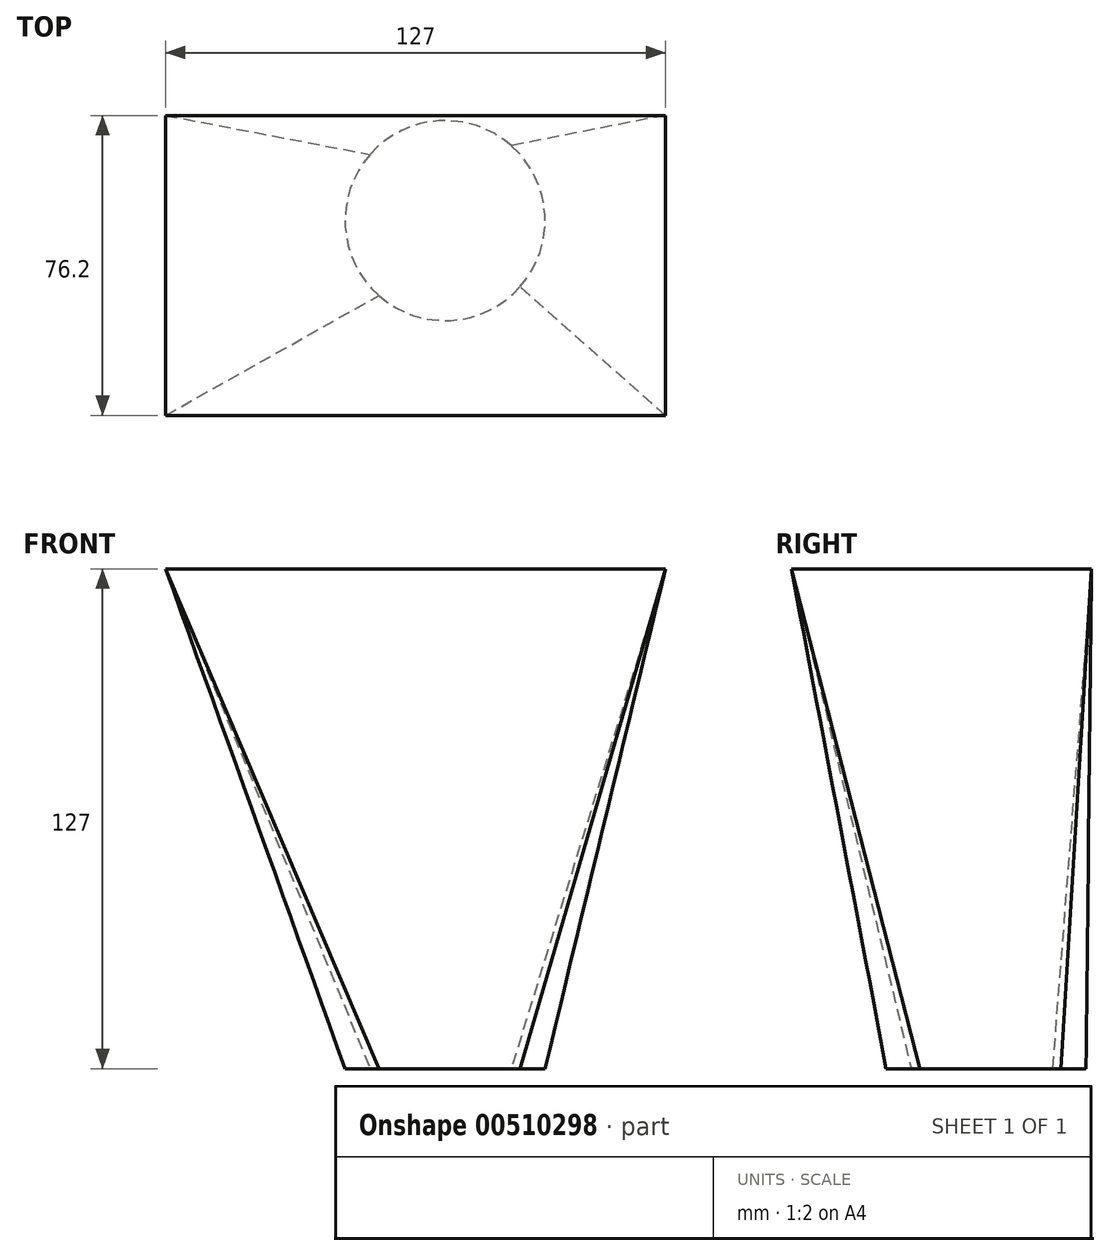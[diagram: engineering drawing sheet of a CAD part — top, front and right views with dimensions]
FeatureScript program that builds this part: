
annotation { "Feature Type Name" : "Feature", "Feature Type Description" : "" }
export const myFeature = defineFeature(function(context is Context, id is Id, definition is map)
    precondition{}
    {
        {
            var Q0;
            Q0=qCreatedBy(makeId("Top.planeOp"),FACE);
            var sketch = newSketch(context, id + "F0", { "sketchPlane" : qUnion([Q0])});
            skCircle(sketch, "E0", {"center": v(0, 11.37) * mm, "radius": 25.4 * mm});
            skSolve(sketch);
        }
        {
            var Q0;
            Q0=qCreatedBy(makeId("Top.planeOp"),FACE);
            cPlane(context, id + "F1", {"entities" : qUnion([Q0]), "cplaneType" : CPlaneType.OFFSET, "offset" : 127 * mm, "width" : 152.4 * mm, "height" : 152.4 * mm});
        }
        {
            var Q0;
            Q0=qCreatedBy(id+"F1.planeOp",FACE);
            var sketch = newSketch(context, id + "F2", { "sketchPlane" : qUnion([Q0])});
            skLineSegment(sketch, "E1.bottom", {"start": v(56, -38.1) * mm, "end": v(-71, -38.1) * mm});
            skLineSegment(sketch, "E1.top", {"start": v(56, 38.1) * mm, "end": v(-71, 38.1) * mm});
            skLineSegment(sketch, "E1.left", {"start": v(56, -38.1) * mm, "end": v(56, 38.1) * mm});
            skLineSegment(sketch, "E1.right", {"start": v(-71, -38.1) * mm, "end": v(-71, 38.1) * mm});
            skPoint(sketch, "E1.middle", {"position": v(-7.5, 0) * mm});
            skSolve(sketch);
        }
        {
            var Q0;
            Q0=makeQuery(id+"F2.imprint","IMPRINT",FACE,{"disambiguationData":[TD([[makeQuery(id+"F2.imprint","IMPRINT",EDGE,{"derivedFrom":sQuery(id+"F2.wireOp",EDGE,"E1.bottom")}),-1.0]])]});
            var Q1;
            Q1=makeQuery(id+"F0.imprint","IMPRINT",FACE,{"disambiguationData":[TD([[makeQuery(id+"F0.imprint","IMPRINT",EDGE,{"derivedFrom":sQuery(id+"F0.wireOp",EDGE,"E0")}),1.0]])]});
            loft(context, id + "F3", {"sheetProfilesArray" : [{ "sheetProfileEntities" : qUnion([Q0]) }, { "sheetProfileEntities" : qUnion([Q1]) }]});
        }
    });
